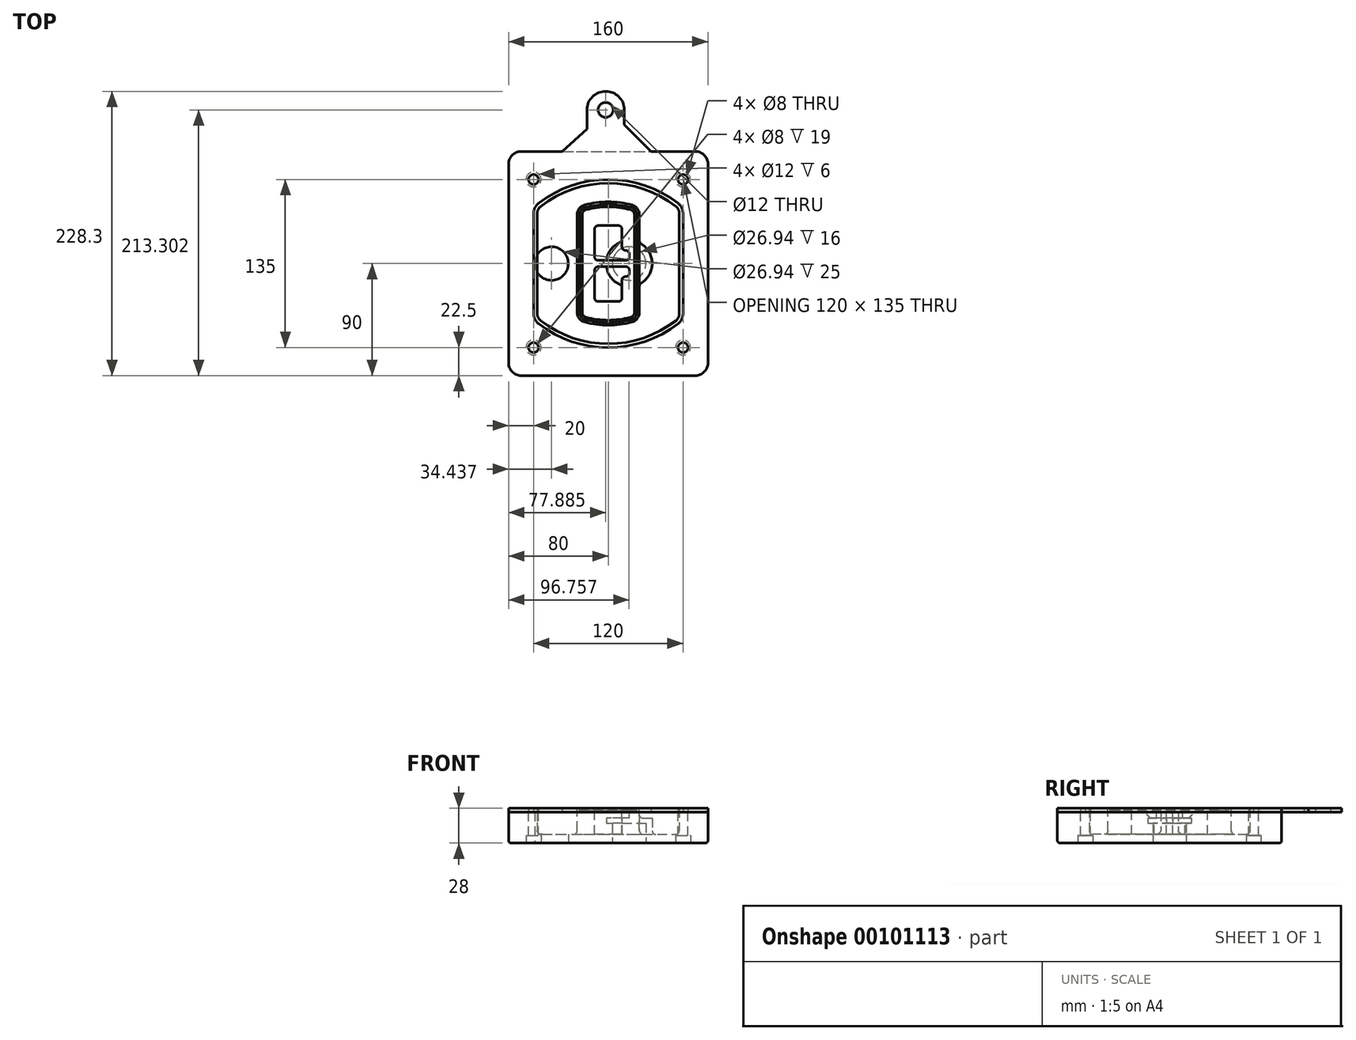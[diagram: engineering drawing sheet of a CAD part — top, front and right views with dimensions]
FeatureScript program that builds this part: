
annotation { "Feature Type Name" : "Feature", "Feature Type Description" : "" }
export const myFeature = defineFeature(function(context is Context, id is Id, definition is map)
    precondition{}
    {
        {
            var Q0;
            Q0=qCreatedBy(makeId("Top.planeOp"),FACE);
            var sketch = newSketch(context, id + "F0", { "sketchPlane" : qUnion([Q0])});
            skPoint(sketch, "E0.rect.middle", {"position": v(0, 0) * mm});
            skLineSegment(sketch, "E1.bottom", {"start": v(-70, -90) * mm, "end": v(70, -90) * mm});
            skLineSegment(sketch, "E1.top", {"start": v(-70, 90) * mm, "end": v(70, 90) * mm});
            skLineSegment(sketch, "E1.left", {"start": v(-80, -80) * mm, "end": v(-80, 80) * mm});
            skLineSegment(sketch, "E1.right", {"start": v(80, -80) * mm, "end": v(80, 80) * mm});
            skLineSegment(sketch, "E2", {"start": v(-80, 90) * mm, "end": v(80, -90) * mm, "construction": true});
            skLineSegment(sketch, "E3", {"start": v(80, 90) * mm, "end": v(-80, -90) * mm, "construction": true});
            skCircle(sketch, "E4", {"center": v(-60, 67.5) * mm, "radius": 4 * mm});
            skCircle(sketch, "E5", {"center": v(60, 67.5) * mm, "radius": 4 * mm});
            skCircle(sketch, "E6", {"center": v(60, -67.5) * mm, "radius": 4 * mm});
            skCircle(sketch, "E7", {"center": v(-60, -67.5) * mm, "radius": 4 * mm});
            skLineSegment(sketch, "E8", {"start": v(-60, 67.5) * mm, "end": v(60, 67.5) * mm, "construction": true});
            skLineSegment(sketch, "E9", {"start": v(60, 67.5) * mm, "end": v(60, -67.5) * mm, "construction": true});
            skLineSegment(sketch, "E10", {"start": v(60, -67.5) * mm, "end": v(-60, -67.5) * mm, "construction": true});
            skLineSegment(sketch, "E11", {"start": v(-60, -67.5) * mm, "end": v(-60, 67.5) * mm, "construction": true});
            skLineSegment(sketch, "E12", {"start": v(-60, 40.3) * mm, "end": v(-60, -40.3) * mm});
            skLineSegment(sketch, "E13", {"start": v(60, 40.3) * mm, "end": v(60, -40.3) * mm});
            skArc(sketch, "E14", {"start": v(56.15, 48.18) * mm, "mid": v(0, 67.5) * mm, "end": v(-56.15, 48.18) * mm});
            skArc(sketch, "E15", {"start": v(-56.15, -48.18) * mm, "mid": v(0, -67.5) * mm, "end": v(56.15, -48.18) * mm});
            skLineSegment(sketch, "E16", {"start": v(-60, 0) * mm, "end": v(60, 0) * mm, "construction": true});
            skPoint(sketch, "E17.visualSharp", {"position": v(-60, -45) * mm});
            skArc(sketch, "E17.filletArc", {"start": v(-60, -40.3) * mm, "mid": v(-58.99, -44.68) * mm, "end": v(-56.15, -48.18) * mm});
            skPoint(sketch, "E18.visualSharp", {"position": v(-60, 45) * mm});
            skArc(sketch, "E18.filletArc", {"start": v(-56.15, 48.18) * mm, "mid": v(-58.99, 44.68) * mm, "end": v(-60, 40.3) * mm});
            skPoint(sketch, "E19.visualSharp", {"position": v(60, 45) * mm});
            skArc(sketch, "E19.filletArc", {"start": v(60, 40.3) * mm, "mid": v(58.99, 44.68) * mm, "end": v(56.15, 48.18) * mm});
            skPoint(sketch, "E20.visualSharp", {"position": v(60, -45) * mm});
            skArc(sketch, "E20.filletArc", {"start": v(56.15, -48.18) * mm, "mid": v(58.99, -44.68) * mm, "end": v(60, -40.3) * mm});
            skPoint(sketch, "E21.visualSharp", {"position": v(-80, 90) * mm});
            skArc(sketch, "E21.filletArc", {"start": v(-70, 90) * mm, "mid": v(-77.07, 87.07) * mm, "end": v(-80, 80) * mm});
            skPoint(sketch, "E22.visualSharp", {"position": v(80, 90) * mm});
            skArc(sketch, "E22.filletArc", {"start": v(80, 80) * mm, "mid": v(77.07, 87.07) * mm, "end": v(70, 90) * mm});
            skPoint(sketch, "E23.visualSharp", {"position": v(80, -90) * mm});
            skArc(sketch, "E23.filletArc", {"start": v(70, -90) * mm, "mid": v(77.07, -87.07) * mm, "end": v(80, -80) * mm});
            skPoint(sketch, "E24.visualSharp", {"position": v(-80, -90) * mm});
            skArc(sketch, "E24.filletArc", {"start": v(-80, -80) * mm, "mid": v(-77.07, -87.07) * mm, "end": v(-70, -90) * mm});
            skArc(sketch, "E25.0", {"start": v(57, 40.3) * mm, "mid": v(56.3, 43.36) * mm, "end": v(54.3, 45.81) * mm});
            skLineSegment(sketch, "E25.1", {"start": v(57, 40.3) * mm, "end": v(57, -40.3) * mm});
            skArc(sketch, "E25.2", {"start": v(54.3, -45.81) * mm, "mid": v(56.3, -43.36) * mm, "end": v(57, -40.3) * mm});
            skArc(sketch, "E25.3", {"start": v(-54.3, -45.81) * mm, "mid": v(0, -64.5) * mm, "end": v(54.3, -45.81) * mm});
            skArc(sketch, "E25.4", {"start": v(-57, -40.3) * mm, "mid": v(-56.3, -43.36) * mm, "end": v(-54.3, -45.81) * mm});
            skArc(sketch, "E25.5", {"start": v(54.3, 45.81) * mm, "mid": v(0, 64.5) * mm, "end": v(-54.3, 45.81) * mm});
            skLineSegment(sketch, "E25.6", {"start": v(-57, 40.3) * mm, "end": v(-57, -40.3) * mm});
            skArc(sketch, "E25.7", {"start": v(-54.3, 45.81) * mm, "mid": v(-56.3, 43.36) * mm, "end": v(-57, 40.3) * mm});
            skArc(sketch, "E26.0", {"start": v(-58.62, 51.33) * mm, "mid": v(-62.58, 46.43) * mm, "end": v(-64, 40.3) * mm});
            skArc(sketch, "E26.1", {"start": v(58.62, 51.33) * mm, "mid": v(0, 71.5) * mm, "end": v(-58.62, 51.33) * mm});
            skArc(sketch, "E26.2", {"start": v(64, 40.3) * mm, "mid": v(62.58, 46.43) * mm, "end": v(58.62, 51.33) * mm});
            skLineSegment(sketch, "E26.3", {"start": v(64, 40.3) * mm, "end": v(64, -40.3) * mm});
            skArc(sketch, "E26.4", {"start": v(58.62, -51.33) * mm, "mid": v(62.58, -46.43) * mm, "end": v(64, -40.3) * mm});
            skLineSegment(sketch, "E26.5", {"start": v(-64, 40.3) * mm, "end": v(-64, -40.3) * mm});
            skArc(sketch, "E26.6", {"start": v(-58.62, -51.33) * mm, "mid": v(0, -71.5) * mm, "end": v(58.62, -51.33) * mm});
            skArc(sketch, "E26.7", {"start": v(-64, -40.3) * mm, "mid": v(-62.58, -46.43) * mm, "end": v(-58.62, -51.33) * mm});
            skSolve(sketch);
        }
        {
            var Q0;
            Q0=makeQuery(id+"F0.imprint","IMPRINT",FACE,{"disambiguationData":[TD([[makeQuery(id+"F0.imprint","IMPRINT",EDGE,{"derivedFrom":sQuery(id+"F0.wireOp",EDGE,"E1.bottom")}),1.0]])]});
            var Q1;
            Q1=makeQuery(id+"F0.imprint","IMPRINT",FACE,{"disambiguationData":[TD([[makeQuery(id+"F0.imprint","IMPRINT",EDGE,{"derivedFrom":sQuery(id+"F0.wireOp",EDGE,"E12")}),1.0]])]});
            var Q2;
            Q2=makeQuery(id+"F0.imprint","IMPRINT",FACE,{"disambiguationData":[TD([[makeQuery(id+"F0.imprint","IMPRINT",EDGE,{"derivedFrom":sQuery(id+"F0.wireOp",EDGE,"E25.0")}),1.0]])]});
            var Q3;
            Q3=makeQuery(id+"F0.imprint","IMPRINT",FACE,{"disambiguationData":[TD([[makeQuery(id+"F0.imprint","IMPRINT",EDGE,{"derivedFrom":sQuery(id+"F0.wireOp",EDGE,"E12")}),-1.0]])]});
            extrude(context, id + "F1", {"entities" : qUnion([Q0, Q1, Q2, Q3]), "oppositeDirection" : true, "depth" : 25 * mm});
        }
        {
            var Q0;
            Q0=makeQuery(id+"F0.imprint","IMPRINT",FACE,{"disambiguationData":[TD([[makeQuery(id+"F0.imprint","IMPRINT",EDGE,{"derivedFrom":sQuery(id+"F0.wireOp",EDGE,"E12")}),1.0]])]});
            extrude(context, id + "F2", {"entities" : qUnion([Q0]), "operationType" : NewBodyOperationType.ADD, "depth" : 3 * mm});
        }
        {
            var Q0;
            Q0=makeQuery(id+"F0.imprint","IMPRINT",FACE,{"disambiguationData":[TD([[makeQuery(id+"F0.imprint","IMPRINT",EDGE,{"derivedFrom":sQuery(id+"F0.wireOp",EDGE,"E25.0")}),1.0]])]});
            extrude(context, id + "F3", {"entities" : qUnion([Q0]), "operationType" : NewBodyOperationType.REMOVE, "oppositeDirection" : true, "depth" : 18 * mm});
        }
        {
            var Q0;
            Q0=makeQuery(id+"F2.opExtrude","CAP_FACE",FACE,{"disambiguationData":[OSD([sQuery(id+"F0.wireOp",EDGE,"E12"),sQuery(id+"F0.wireOp",EDGE,"E13"),sQuery(id+"F0.wireOp",EDGE,"E14"),sQuery(id+"F0.wireOp",EDGE,"E15"),sQuery(id+"F0.wireOp",EDGE,"E17.filletArc"),sQuery(id+"F0.wireOp",EDGE,"E18.filletArc"),sQuery(id+"F0.wireOp",EDGE,"E19.filletArc"),sQuery(id+"F0.wireOp",EDGE,"E20.filletArc"),sQuery(id+"F0.wireOp",EDGE,"E25.0"),sQuery(id+"F0.wireOp",EDGE,"E25.1"),sQuery(id+"F0.wireOp",EDGE,"E25.2"),sQuery(id+"F0.wireOp",EDGE,"E25.3"),sQuery(id+"F0.wireOp",EDGE,"E25.4"),sQuery(id+"F0.wireOp",EDGE,"E25.5"),sQuery(id+"F0.wireOp",EDGE,"E25.6"),sQuery(id+"F0.wireOp",EDGE,"E25.7")])],"isStart":false});
            var sketch = newSketch(context, id + "F4", { "sketchPlane" : qUnion([Q0])});
            skArc(sketch, "E27.0", {"start": v(-19.08, -46.97) * mm, "mid": v(0, -49.5) * mm, "end": v(19.08, -46.97) * mm});
            skArc(sketch, "E28.0", {"start": v(19.08, 46.97) * mm, "mid": v(0, 49.5) * mm, "end": v(-19.08, 46.97) * mm});
            skLineSegment(sketch, "E29", {"start": v(-25, 39.25) * mm, "end": v(-25, -39.25) * mm});
            skLineSegment(sketch, "E30", {"start": v(25, 39.25) * mm, "end": v(25, -39.25) * mm});
            skLineSegment(sketch, "E31", {"start": v(-25, 45.1) * mm, "end": v(25, 45.1) * mm, "construction": true});
            skLineSegment(sketch, "E32", {"start": v(-25, -45.1) * mm, "end": v(25, -45.1) * mm, "construction": true});
            skPoint(sketch, "E33.visualSharp", {"position": v(-25, 45.1) * mm});
            skArc(sketch, "E33.filletArc", {"start": v(-19.08, 46.97) * mm, "mid": v(-23.35, 44.11) * mm, "end": v(-25, 39.25) * mm});
            skPoint(sketch, "E34.visualSharp", {"position": v(25, 45.1) * mm});
            skArc(sketch, "E34.filletArc", {"start": v(25, 39.25) * mm, "mid": v(23.35, 44.11) * mm, "end": v(19.08, 46.97) * mm});
            skPoint(sketch, "E35.visualSharp", {"position": v(25, -45.1) * mm});
            skArc(sketch, "E35.filletArc", {"start": v(19.08, -46.97) * mm, "mid": v(23.35, -44.11) * mm, "end": v(25, -39.25) * mm});
            skPoint(sketch, "E36.visualSharp", {"position": v(-25, -45.1) * mm});
            skArc(sketch, "E36.filletArc", {"start": v(-25, -39.25) * mm, "mid": v(-23.35, -44.11) * mm, "end": v(-19.08, -46.97) * mm});
            skArc(sketch, "E37.0", {"start": v(54.3, 45.81) * mm, "mid": v(0, 64.5) * mm, "end": v(-54.3, 45.81) * mm});
            skArc(sketch, "E37.1", {"start": v(-54.3, 45.81) * mm, "mid": v(-56.3, 43.36) * mm, "end": v(-57, 40.3) * mm});
            skLineSegment(sketch, "E37.2", {"start": v(-57, 40.3) * mm, "end": v(-57, -40.3) * mm});
            skArc(sketch, "E37.3", {"start": v(-57, -40.3) * mm, "mid": v(-56.3, -43.36) * mm, "end": v(-54.3, -45.81) * mm});
            skArc(sketch, "E37.4", {"start": v(-54.3, -45.81) * mm, "mid": v(0, -64.5) * mm, "end": v(54.3, -45.81) * mm});
            skArc(sketch, "E37.5", {"start": v(54.3, -45.81) * mm, "mid": v(56.3, -43.36) * mm, "end": v(57, -40.3) * mm});
            skLineSegment(sketch, "E37.6", {"start": v(57, 40.3) * mm, "end": v(57, -40.3) * mm});
            skArc(sketch, "E37.7", {"start": v(57, 40.3) * mm, "mid": v(56.3, 43.36) * mm, "end": v(54.3, 45.81) * mm});
            skLineSegment(sketch, "E38.0", {"start": v(23, 39.25) * mm, "end": v(23, -39.25) * mm});
            skArc(sketch, "E38.1", {"start": v(18.56, -45.04) * mm, "mid": v(21.76, -42.9) * mm, "end": v(23, -39.25) * mm});
            skArc(sketch, "E38.2", {"start": v(-18.56, -45.04) * mm, "mid": v(0, -47.5) * mm, "end": v(18.56, -45.04) * mm});
            skArc(sketch, "E38.3", {"start": v(-23, -39.25) * mm, "mid": v(-21.76, -42.9) * mm, "end": v(-18.56, -45.04) * mm});
            skLineSegment(sketch, "E38.4", {"start": v(-23, 39.25) * mm, "end": v(-23, -39.25) * mm});
            skArc(sketch, "E38.5", {"start": v(23, 39.25) * mm, "mid": v(21.76, 42.9) * mm, "end": v(18.56, 45.04) * mm});
            skArc(sketch, "E38.6", {"start": v(-18.56, 45.04) * mm, "mid": v(-21.76, 42.9) * mm, "end": v(-23, 39.25) * mm});
            skArc(sketch, "E38.7", {"start": v(18.56, 45.04) * mm, "mid": v(0, 47.5) * mm, "end": v(-18.56, 45.04) * mm});
            skArc(sketch, "E39.0", {"start": v(21, 39.25) * mm, "mid": v(20.18, 41.68) * mm, "end": v(18.04, 43.1) * mm});
            skLineSegment(sketch, "E39.1", {"start": v(21, 39.25) * mm, "end": v(21, -39.25) * mm});
            skArc(sketch, "E39.2", {"start": v(18.04, -43.1) * mm, "mid": v(20.18, -41.68) * mm, "end": v(21, -39.25) * mm});
            skArc(sketch, "E39.3", {"start": v(-18.04, -43.1) * mm, "mid": v(0, -45.5) * mm, "end": v(18.04, -43.1) * mm});
            skArc(sketch, "E39.4", {"start": v(-21, -39.25) * mm, "mid": v(-20.18, -41.68) * mm, "end": v(-18.04, -43.1) * mm});
            skArc(sketch, "E39.5", {"start": v(18.04, 43.1) * mm, "mid": v(0, 45.5) * mm, "end": v(-18.04, 43.1) * mm});
            skLineSegment(sketch, "E39.6", {"start": v(-21, 39.25) * mm, "end": v(-21, -39.25) * mm});
            skArc(sketch, "E39.7", {"start": v(-18.04, 43.1) * mm, "mid": v(-20.18, 41.68) * mm, "end": v(-21, 39.25) * mm});
            skLineSegment(sketch, "E40", {"start": v(-25, 0) * mm, "end": v(25, 0) * mm, "construction": true});
            skLineSegment(sketch, "E41", {"start": v(-11, 5.5) * mm, "end": v(-11, 27.5) * mm});
            skLineSegment(sketch, "E42", {"start": v(-8, 30.5) * mm, "end": v(8, 30.5) * mm});
            skLineSegment(sketch, "E43", {"start": v(11, 27.5) * mm, "end": v(11, 13.5) * mm});
            skLineSegment(sketch, "E44", {"start": v(14, 10.5) * mm, "end": v(14, 10.5) * mm});
            skLineSegment(sketch, "E45", {"start": v(17, 7.5) * mm, "end": v(17, 5.5) * mm});
            skLineSegment(sketch, "E46", {"start": v(14, 2.5) * mm, "end": v(-8, 2.5) * mm});
            skPoint(sketch, "E47.visualSharp", {"position": v(-11, 30.5) * mm});
            skArc(sketch, "E47.filletArc", {"start": v(-8, 30.5) * mm, "mid": v(-10.12, 29.62) * mm, "end": v(-11, 27.5) * mm});
            skPoint(sketch, "E48.visualSharp", {"position": v(11, 30.5) * mm});
            skArc(sketch, "E48.filletArc", {"start": v(11, 27.5) * mm, "mid": v(10.12, 29.62) * mm, "end": v(8, 30.5) * mm});
            skPoint(sketch, "E49.visualSharp", {"position": v(11, 10.5) * mm});
            skArc(sketch, "E49.filletArc", {"start": v(11, 13.5) * mm, "mid": v(11.88, 11.38) * mm, "end": v(14, 10.5) * mm});
            skPoint(sketch, "E50.visualSharp", {"position": v(17, 10.5) * mm});
            skArc(sketch, "E50.filletArc", {"start": v(17, 7.5) * mm, "mid": v(16.12, 9.62) * mm, "end": v(14, 10.5) * mm});
            skPoint(sketch, "E51.visualSharp", {"position": v(17, 2.5) * mm});
            skArc(sketch, "E51.filletArc", {"start": v(14, 2.5) * mm, "mid": v(16.12, 3.38) * mm, "end": v(17, 5.5) * mm});
            skPoint(sketch, "E52.visualSharp", {"position": v(-11, 2.5) * mm});
            skArc(sketch, "E52.filletArc", {"start": v(-11, 5.5) * mm, "mid": v(-10.12, 3.38) * mm, "end": v(-8, 2.5) * mm});
            skLineSegment(sketch, "E53.0.MirrorCS", {"start": v(14, -2.5) * mm, "end": v(-8, -2.5) * mm});
            skArc(sketch, "E54.0.MirrorCS", {"start": v(-11, -5.5) * mm, "mid": v(-10.12, -3.38) * mm, "end": v(-8, -2.5) * mm});
            skLineSegment(sketch, "E55.0.MirrorCS", {"start": v(-11, -5.5) * mm, "end": v(-11, -27.5) * mm});
            skArc(sketch, "E56.0.MirrorCS", {"start": v(-8, -30.5) * mm, "mid": v(-10.12, -29.62) * mm, "end": v(-11, -27.5) * mm});
            skLineSegment(sketch, "E57.0.MirrorCS", {"start": v(-8, -30.5) * mm, "end": v(8, -30.5) * mm});
            skArc(sketch, "E58.0.MirrorCS", {"start": v(11, -27.5) * mm, "mid": v(10.12, -29.62) * mm, "end": v(8, -30.5) * mm});
            skLineSegment(sketch, "E59.0.MirrorCS", {"start": v(11, -27.5) * mm, "end": v(11, -13.5) * mm});
            skArc(sketch, "E60.0.MirrorCS", {"start": v(11, -13.5) * mm, "mid": v(11.88, -11.38) * mm, "end": v(14, -10.5) * mm});
            skArc(sketch, "E61.0.MirrorCS", {"start": v(17, -7.5) * mm, "mid": v(16.12, -9.62) * mm, "end": v(14, -10.5) * mm});
            skLineSegment(sketch, "E62.0.MirrorCS", {"start": v(17, -7.5) * mm, "end": v(17, -5.5) * mm});
            skArc(sketch, "E63.0.MirrorCS", {"start": v(14, -2.5) * mm, "mid": v(16.12, -3.38) * mm, "end": v(17, -5.5) * mm});
            skSolve(sketch);
        }
        {
            var Q0;
            Q0=makeQuery(id+"F4.imprint","IMPRINT",FACE,{"disambiguationData":[TD([[makeQuery(id+"F4.imprint","IMPRINT",EDGE,{"derivedFrom":sQuery(id+"F4.wireOp",EDGE,"E27.0")}),1.0]])]});
            var Q1;
            Q1=makeQuery(id+"F4.imprint","IMPRINT",FACE,{"disambiguationData":[TD([[makeQuery(id+"F4.imprint","IMPRINT",EDGE,{"derivedFrom":sQuery(id+"F4.wireOp",EDGE,"E38.0")}),-1.0]])]});
            var Q2;
            Q2=makeQuery(id+"F4.imprint","IMPRINT",FACE,{"disambiguationData":[TD([[makeQuery(id+"F4.imprint","IMPRINT",EDGE,{"derivedFrom":sQuery(id+"F4.wireOp",EDGE,"E39.0")}),1.0]])]});
            extrude(context, id + "F5", {"entities" : qUnion([Q0, Q1, Q2]), "operationType" : NewBodyOperationType.ADD, "endBound" : BoundingType.UP_TO_NEXT, "oppositeDirection" : true, "depth" : 25 * mm});
        }
        {
            var Q0;
            Q0=makeQuery(id+"F4.imprint","IMPRINT",FACE,{"disambiguationData":[TD([[makeQuery(id+"F4.imprint","IMPRINT",EDGE,{"derivedFrom":sQuery(id+"F4.wireOp",EDGE,"E38.0")}),-1.0]])]});
            extrude(context, id + "F6", {"entities" : qUnion([Q0]), "operationType" : NewBodyOperationType.REMOVE, "oppositeDirection" : true, "depth" : 2 * mm});
        }
        {
            var Q0;
            Q0=makeQuery(id+"F1.opExtrude","CAP_FACE",FACE,{"disambiguationData":[OSD([sQuery(id+"F0.wireOp",EDGE,"E1.bottom"),sQuery(id+"F0.wireOp",EDGE,"E1.top"),sQuery(id+"F0.wireOp",EDGE,"E1.left"),sQuery(id+"F0.wireOp",EDGE,"E1.right"),sQuery(id+"F0.wireOp",EDGE,"E4"),sQuery(id+"F0.wireOp",EDGE,"E5"),sQuery(id+"F0.wireOp",EDGE,"E6"),sQuery(id+"F0.wireOp",EDGE,"E7"),sQuery(id+"F0.wireOp",EDGE,"E21.filletArc"),sQuery(id+"F0.wireOp",EDGE,"E22.filletArc"),sQuery(id+"F0.wireOp",EDGE,"E23.filletArc"),sQuery(id+"F0.wireOp",EDGE,"E24.filletArc")])],"isStart":false});
            var sketch = newSketch(context, id + "F7", { "sketchPlane" : qUnion([Q0])});
            skCircle(sketch, "E64", {"center": v(16.76, 0) * mm, "radius": 13.47 * mm});
            skCircle(sketch, "E65", {"center": v(-45.56, 0) * mm, "radius": 13.47 * mm});
            skLineSegment(sketch, "E66", {"start": v(80, 0) * mm, "end": v(-80, 0) * mm});
            skCircle(sketch, "E67", {"center": v(16.76, 0) * mm, "radius": 18.47 * mm});
            skCircle(sketch, "E68", {"center": v(60, -67.5) * mm, "radius": 6 * mm});
            skCircle(sketch, "E69", {"center": v(-60, -67.5) * mm, "radius": 6 * mm});
            skCircle(sketch, "E70", {"center": v(-60, 67.5) * mm, "radius": 6 * mm});
            skCircle(sketch, "E71", {"center": v(60, 67.5) * mm, "radius": 6 * mm});
            skSolve(sketch);
        }
        {
            var Q0;
            {var subQ1=sQuery(id+"F7.wireOp",EDGE,"E66");var subQ4=sQuery(id+"F7.wireOp",EDGE,"E64");var subQ6=makeQuery(id+"F7.imprint","INTERSECT",VERTEX,{"disambiguationData":[OD(0.0)],"derivedFrom":[subQ4,subQ1]});Q0=makeQuery(id+"F7.imprint","IMPRINT",FACE,{"disambiguationData":[TD([[makeQuery(id+"F7.imprint","IMPRINT",EDGE,{"disambiguationData":[TD([[subQ6,-1.0]])],"derivedFrom":subQ4}),-1.0]])]});}
            var Q1;
            {var subQ0=sQuery(id+"F7.wireOp",EDGE,"E66");var subQ1=sQuery(id+"F7.wireOp",EDGE,"E64");var subQ3=makeQuery(id+"F7.imprint","INTERSECT",VERTEX,{"disambiguationData":[OD(0.0)],"derivedFrom":[subQ1,subQ0]});Q1=makeQuery(id+"F7.imprint","IMPRINT",FACE,{"disambiguationData":[TD([[makeQuery(id+"F7.imprint","IMPRINT",EDGE,{"disambiguationData":[TD([[subQ3,-1.0]])],"derivedFrom":subQ1}),1.0]])]});}
            var Q2;
            {var subQ0=sQuery(id+"F7.wireOp",EDGE,"E66");var subQ1=sQuery(id+"F7.wireOp",EDGE,"E64");var subQ3=makeQuery(id+"F7.imprint","INTERSECT",VERTEX,{"disambiguationData":[OD(0.0)],"derivedFrom":[subQ1,subQ0]});Q2=makeQuery(id+"F7.imprint","IMPRINT",FACE,{"disambiguationData":[TD([[makeQuery(id+"F7.imprint","IMPRINT",EDGE,{"disambiguationData":[TD([[subQ3,1.0]])],"derivedFrom":subQ1}),1.0]])]});}
            var Q3;
            {var subQ1=sQuery(id+"F7.wireOp",EDGE,"E66");var subQ4=sQuery(id+"F7.wireOp",EDGE,"E64");var subQ6=makeQuery(id+"F7.imprint","INTERSECT",VERTEX,{"disambiguationData":[OD(0.0)],"derivedFrom":[subQ4,subQ1]});Q3=makeQuery(id+"F7.imprint","IMPRINT",FACE,{"disambiguationData":[TD([[makeQuery(id+"F7.imprint","IMPRINT",EDGE,{"disambiguationData":[TD([[subQ6,1.0]])],"derivedFrom":subQ4}),-1.0]])]});}
            extrude(context, id + "F8", {"entities" : qUnion([Q0, Q1, Q2, Q3]), "operationType" : NewBodyOperationType.ADD, "oppositeDirection" : true, "depth" : 20 * mm});
        }
        {
            var Q0;
            {var subQ0=sQuery(id+"F7.wireOp",EDGE,"E66");var subQ1=sQuery(id+"F7.wireOp",EDGE,"E64");var subQ3=makeQuery(id+"F7.imprint","INTERSECT",VERTEX,{"disambiguationData":[OD(0.0)],"derivedFrom":[subQ1,subQ0]});Q0=makeQuery(id+"F7.imprint","IMPRINT",FACE,{"disambiguationData":[TD([[makeQuery(id+"F7.imprint","IMPRINT",EDGE,{"disambiguationData":[TD([[subQ3,-1.0]])],"derivedFrom":subQ1}),1.0]])]});}
            var Q1;
            {var subQ0=sQuery(id+"F7.wireOp",EDGE,"E66");var subQ1=sQuery(id+"F7.wireOp",EDGE,"E64");var subQ3=makeQuery(id+"F7.imprint","INTERSECT",VERTEX,{"disambiguationData":[OD(0.0)],"derivedFrom":[subQ1,subQ0]});Q1=makeQuery(id+"F7.imprint","IMPRINT",FACE,{"disambiguationData":[TD([[makeQuery(id+"F7.imprint","IMPRINT",EDGE,{"disambiguationData":[TD([[subQ3,1.0]])],"derivedFrom":subQ1}),1.0]])]});}
            extrude(context, id + "F9", {"entities" : qUnion([Q0, Q1]), "operationType" : NewBodyOperationType.REMOVE, "oppositeDirection" : true, "depth" : 16 * mm});
        }
        {
            var Q0;
            {var subQ0=sQuery(id+"F7.wireOp",EDGE,"E66");var subQ1=sQuery(id+"F7.wireOp",EDGE,"E65");var subQ3=makeQuery(id+"F7.imprint","INTERSECT",VERTEX,{"disambiguationData":[OD(0.0)],"derivedFrom":[subQ1,subQ0]});Q0=makeQuery(id+"F7.imprint","IMPRINT",FACE,{"disambiguationData":[TD([[makeQuery(id+"F7.imprint","IMPRINT",EDGE,{"disambiguationData":[TD([[subQ3,-1.0]])],"derivedFrom":subQ1}),1.0]])]});}
            var Q1;
            {var subQ0=sQuery(id+"F7.wireOp",EDGE,"E66");var subQ1=sQuery(id+"F7.wireOp",EDGE,"E65");var subQ3=makeQuery(id+"F7.imprint","INTERSECT",VERTEX,{"disambiguationData":[OD(0.0)],"derivedFrom":[subQ1,subQ0]});Q1=makeQuery(id+"F7.imprint","IMPRINT",FACE,{"disambiguationData":[TD([[makeQuery(id+"F7.imprint","IMPRINT",EDGE,{"disambiguationData":[TD([[subQ3,1.0]])],"derivedFrom":subQ1}),1.0]])]});}
            extrude(context, id + "F10", {"entities" : qUnion([Q0, Q1]), "operationType" : NewBodyOperationType.REMOVE, "oppositeDirection" : true, "depth" : 25 * mm});
        }
        {
            var Q0;
            Q0=makeQuery(id+"F7.imprint","IMPRINT",FACE,{"disambiguationData":[TD([[makeQuery(id+"F7.imprint","IMPRINT",EDGE,{"derivedFrom":sQuery(id+"F7.wireOp",EDGE,"E68")}),1.0]])]});
            var Q1;
            Q1=makeQuery(id+"F7.imprint","IMPRINT",FACE,{"disambiguationData":[TD([[makeQuery(id+"F7.imprint","IMPRINT",EDGE,{"derivedFrom":makeQuery(id+"F1.opExtrude","CAP_EDGE",EDGE,{"disambiguationData":[OSD([sQuery(id+"F0.wireOp",EDGE,"E5")])],"isStart":false})}),-1.0]])]});
            var Q2;
            Q2=makeQuery(id+"F7.imprint","IMPRINT",FACE,{"disambiguationData":[TD([[makeQuery(id+"F7.imprint","IMPRINT",EDGE,{"derivedFrom":sQuery(id+"F7.wireOp",EDGE,"E69")}),1.0]])]});
            var Q3;
            Q3=makeQuery(id+"F7.imprint","IMPRINT",FACE,{"disambiguationData":[TD([[makeQuery(id+"F7.imprint","IMPRINT",EDGE,{"derivedFrom":makeQuery(id+"F1.opExtrude","CAP_EDGE",EDGE,{"disambiguationData":[OSD([sQuery(id+"F0.wireOp",EDGE,"E4")])],"isStart":false})}),-1.0]])]});
            var Q4;
            Q4=makeQuery(id+"F7.imprint","IMPRINT",FACE,{"disambiguationData":[TD([[makeQuery(id+"F7.imprint","IMPRINT",EDGE,{"derivedFrom":sQuery(id+"F7.wireOp",EDGE,"E70")}),1.0]])]});
            var Q5;
            Q5=makeQuery(id+"F7.imprint","IMPRINT",FACE,{"disambiguationData":[TD([[makeQuery(id+"F7.imprint","IMPRINT",EDGE,{"derivedFrom":makeQuery(id+"F1.opExtrude","CAP_EDGE",EDGE,{"disambiguationData":[OSD([sQuery(id+"F0.wireOp",EDGE,"E7")])],"isStart":false})}),-1.0]])]});
            var Q6;
            Q6=makeQuery(id+"F7.imprint","IMPRINT",FACE,{"disambiguationData":[TD([[makeQuery(id+"F7.imprint","IMPRINT",EDGE,{"derivedFrom":sQuery(id+"F7.wireOp",EDGE,"E71")}),1.0]])]});
            var Q7;
            Q7=makeQuery(id+"F7.imprint","IMPRINT",FACE,{"disambiguationData":[TD([[makeQuery(id+"F7.imprint","IMPRINT",EDGE,{"derivedFrom":makeQuery(id+"F1.opExtrude","CAP_EDGE",EDGE,{"disambiguationData":[OSD([sQuery(id+"F0.wireOp",EDGE,"E6")])],"isStart":false})}),-1.0]])]});
            extrude(context, id + "F11", {"entities" : qUnion([Q0, Q1, Q2, Q3, Q4, Q5, Q6, Q7]), "operationType" : NewBodyOperationType.REMOVE, "oppositeDirection" : true, "depth" : 6 * mm});
        }
        {
            var Q0;
            Q0=makeQuery(id+"F9.boolean.opBoolean","COPY",FACE,{"derivedFrom":makeQuery(id+"F9.opExtrude","CAP_FACE",FACE,{"disambiguationData":[OSD([sQuery(id+"F7.wireOp",EDGE,"E64")])],"isStart":false})});
            var sketch = newSketch(context, id + "F12", { "sketchPlane" : qUnion([Q0])});
            skArc(sketch, "E72.0", {"start": v(11, 17.55) * mm, "mid": v(2.57, 11.82) * mm, "end": v(-1.54, 2.5) * mm});
            skArc(sketch, "E72.1", {"start": v(-1.54, -2.5) * mm, "mid": v(2.57, -11.82) * mm, "end": v(11, -17.55) * mm});
            skLineSegment(sketch, "E73", {"start": v(-1.54, -2.5) * mm, "end": v(14, -2.5) * mm});
            skLineSegment(sketch, "E74.0", {"start": v(14, 2.5) * mm, "end": v(-1.54, 2.5) * mm});
            skArc(sketch, "E74.1", {"start": v(14, 2.5) * mm, "mid": v(16.12, 3.38) * mm, "end": v(17, 5.5) * mm});
            skLineSegment(sketch, "E74.2", {"start": v(17, 7.5) * mm, "end": v(17, 5.5) * mm});
            skArc(sketch, "E74.3", {"start": v(17, 7.5) * mm, "mid": v(16.12, 9.62) * mm, "end": v(14, 10.5) * mm});
            skArc(sketch, "E74.4", {"start": v(11, 13.5) * mm, "mid": v(11.88, 11.38) * mm, "end": v(14, 10.5) * mm});
            skLineSegment(sketch, "E74.5", {"start": v(11, 17.55) * mm, "end": v(11, 13.5) * mm});
            skLineSegment(sketch, "E74.7", {"start": v(14, -2.5) * mm, "end": v(-1.54, -2.5) * mm});
            skArc(sketch, "E74.8", {"start": v(14, -2.5) * mm, "mid": v(16.12, -3.38) * mm, "end": v(17, -5.5) * mm});
            skLineSegment(sketch, "E74.9", {"start": v(17, -7.5) * mm, "end": v(17, -5.5) * mm});
            skArc(sketch, "E74.10", {"start": v(17, -7.5) * mm, "mid": v(16.12, -9.62) * mm, "end": v(14, -10.5) * mm});
            skArc(sketch, "E74.11", {"start": v(11, -13.5) * mm, "mid": v(11.88, -11.38) * mm, "end": v(14, -10.5) * mm});
            skLineSegment(sketch, "E74.12", {"start": v(11, -17.55) * mm, "end": v(11, -13.5) * mm});
            skPoint(sketch, "E75.orphan", {"position": v(11, -27.5) * mm});
            skPoint(sketch, "E76.orphan", {"position": v(-8, -2.5) * mm});
            skPoint(sketch, "E77.orphan", {"position": v(-8, 2.5) * mm});
            skPoint(sketch, "E78.orphan", {"position": v(11, 27.5) * mm});
            skSolve(sketch);
        }
        {
            var Q0;
            {var subQ7=sQuery(id+"F12.wireOp",EDGE,"E72.0");var subQ14=sQuery(id+"F12.wireOp",EDGE,"E72.1");var subQ16=sQuery(id+"F12.wireOp",EDGE,"E74.1");var subQ18=sQuery(id+"F12.wireOp",EDGE,"E74.8");Q0=qUnion([makeQuery(id+"F12.imprint","IMPRINT",FACE,{"disambiguationData":[TD([[makeQuery(id+"F12.imprint","IMPRINT",EDGE,{"derivedFrom":subQ7}),1.0]])]}),makeQuery(id+"F12.imprint","IMPRINT",FACE,{"disambiguationData":[TD([[makeQuery(id+"F12.imprint","IMPRINT",EDGE,{"derivedFrom":subQ14}),1.0]])]}),makeQuery(id+"F12.imprint","IMPRINT",FACE,{"disambiguationData":[TD([[makeQuery(id+"F12.imprint","IMPRINT",EDGE,{"derivedFrom":subQ16}),1.0]])]}),makeQuery(id+"F12.imprint","IMPRINT",FACE,{"disambiguationData":[TD([[makeQuery(id+"F12.imprint","IMPRINT",EDGE,{"derivedFrom":subQ18}),-1.0]])]})]);}
            var Q1;
            Q1=makeQuery(id+"F5.boolean.opBoolean","SPLIT",FACE,{"disambiguationData":[TD([makeQuery(id+"F5.opExtrude","SWEPT_FACE",FACE,{"disambiguationData":[OSD([sQuery(id+"F4.wireOp",EDGE,"E41")])]})])],"derivedFrom":makeQuery(id+"F3.boolean.opBoolean","COPY",FACE,{"derivedFrom":makeQuery(id+"F3.opExtrude","CAP_FACE",FACE,{"disambiguationData":[OSD([sQuery(id+"F0.wireOp",EDGE,"E25.0"),sQuery(id+"F0.wireOp",EDGE,"E25.1"),sQuery(id+"F0.wireOp",EDGE,"E25.2"),sQuery(id+"F0.wireOp",EDGE,"E25.3"),sQuery(id+"F0.wireOp",EDGE,"E25.4"),sQuery(id+"F0.wireOp",EDGE,"E25.5"),sQuery(id+"F0.wireOp",EDGE,"E25.6"),sQuery(id+"F0.wireOp",EDGE,"E25.7")])],"isStart":false})})});
            extrude(context, id + "F13", {"entities" : qUnion([Q0]), "operationType" : NewBodyOperationType.REMOVE, "endBound" : BoundingType.UP_TO_SURFACE, "endBoundEntityFace" : qUnion([Q1]), "depth" : 25 * mm});
        }
        {
            var Q0;
            Q0=makeQuery(id+"F3.boolean.opBoolean","COPY",EDGE,{"derivedFrom":makeQuery(id+"F3.opExtrude","CAP_EDGE",EDGE,{"disambiguationData":[OSD([sQuery(id+"F0.wireOp",EDGE,"E25.6")])],"isStart":false})});
            var Q1;
            Q1=makeQuery(id+"F8.boolean.opBoolean","INTERSECT",EDGE,{"derivedFrom":[makeQuery(id+"F5.opExtrude","SWEPT_FACE",FACE,{"disambiguationData":[OSD([sQuery(id+"F4.wireOp",EDGE,"E30")])]}),makeQuery(id+"F8.opExtrude","CAP_FACE",FACE,{"disambiguationData":[OSD([sQuery(id+"F7.wireOp",EDGE,"E67")])],"isStart":false})]});
            var Q2;
            Q2=makeQuery(id+"F8.boolean.opBoolean","INTERSECT",EDGE,{"disambiguationData":[OD(1.0)],"derivedFrom":[makeQuery(id+"F5.opExtrude","SWEPT_FACE",FACE,{"disambiguationData":[OSD([sQuery(id+"F4.wireOp",EDGE,"E30")])]}),makeQuery(id+"F8.opExtrude","SWEPT_FACE",FACE,{"disambiguationData":[OSD([sQuery(id+"F7.wireOp",EDGE,"E67")])]})]});
            var Q3;
            {var subQ0=sQuery(id+"F4.wireOp",EDGE,"E30");Q3=makeQuery(id+"F8.boolean.opBoolean","SPLIT",EDGE,{"disambiguationData":[TD([makeQuery(id+"F5.opExtrude","SWEPT_FACE",FACE,{"disambiguationData":[OSD([sQuery(id+"F4.wireOp",EDGE,"E35.filletArc")])]})])],"derivedFrom":makeQuery(id+"F5.opExtrude","CAP_EDGE",EDGE,{"disambiguationData":[OSD([subQ0])],"isStart":false})});}
            var Q4;
            {var subQ0=sQuery(id+"F0.wireOp",EDGE,"E25.7");var subQ1=sQuery(id+"F0.wireOp",EDGE,"E25.1");var subQ2=sQuery(id+"F0.wireOp",EDGE,"E25.6");var subQ3=sQuery(id+"F0.wireOp",EDGE,"E25.5");var subQ4=sQuery(id+"F0.wireOp",EDGE,"E25.4");var subQ5=sQuery(id+"F0.wireOp",EDGE,"E25.0");var subQ6=sQuery(id+"F0.wireOp",EDGE,"E25.2");var subQ7=sQuery(id+"F0.wireOp",EDGE,"E25.3");Q4=makeQuery(id+"F8.boolean.opBoolean","INTERSECT",EDGE,{"derivedFrom":[makeQuery(id+"F5.boolean.opBoolean","SPLIT",FACE,{"disambiguationData":[TD([makeQuery(id+"F2.opExtrude","SWEPT_FACE",FACE,{"disambiguationData":[OSD([subQ5])]})])],"derivedFrom":makeQuery(id+"F3.boolean.opBoolean","COPY",FACE,{"derivedFrom":makeQuery(id+"F3.opExtrude","CAP_FACE",FACE,{"disambiguationData":[OSD([subQ5,subQ1,subQ6,subQ7,subQ4,subQ3,subQ2,subQ0])],"isStart":false})})}),makeQuery(id+"F8.opExtrude","SWEPT_FACE",FACE,{"disambiguationData":[OSD([sQuery(id+"F7.wireOp",EDGE,"E67")])]})]});}
            var Q5;
            Q5=makeQuery(id+"F8.boolean.opBoolean","INTERSECT",EDGE,{"disambiguationData":[OD(0.0)],"derivedFrom":[makeQuery(id+"F5.opExtrude","SWEPT_FACE",FACE,{"disambiguationData":[OSD([sQuery(id+"F4.wireOp",EDGE,"E30")])]}),makeQuery(id+"F8.opExtrude","SWEPT_FACE",FACE,{"disambiguationData":[OSD([sQuery(id+"F7.wireOp",EDGE,"E67")])]})]});
            fillet(context, id + "F14", {"entities" : qUnion([Q0, Q1, Q2, Q3, Q4, Q5]), "radius" : 3 * mm, "tangentPropagation" : true, "allowEdgeOverflow" : false});
        }
        {
            var Q0;
            Q0=makeQuery(id+"F1.opExtrude","CAP_EDGE",EDGE,{"disambiguationData":[OSD([sQuery(id+"F0.wireOp",EDGE,"E1.bottom")])],"isStart":false});
            fillet(context, id + "F15", {"entities" : qUnion([Q0]), "radius" : 2 * mm, "tangentPropagation" : true, "allowEdgeOverflow" : false});
        }
        {
            var Q0;
            {var subQ0=sQuery(id+"F0.wireOp",EDGE,"E22.filletArc");var subQ1=sQuery(id+"F0.wireOp",EDGE,"E7");var subQ2=sQuery(id+"F0.wireOp",EDGE,"E6");var subQ3=sQuery(id+"F0.wireOp",EDGE,"E5");var subQ4=sQuery(id+"F0.wireOp",EDGE,"E4");var subQ5=sQuery(id+"F0.wireOp",EDGE,"E1.bottom");var subQ6=sQuery(id+"F0.wireOp",EDGE,"E21.filletArc");var subQ7=sQuery(id+"F0.wireOp",EDGE,"E1.top");var subQ8=sQuery(id+"F0.wireOp",EDGE,"E1.left");var subQ9=sQuery(id+"F0.wireOp",EDGE,"E1.right");var subQ10=sQuery(id+"F0.wireOp",EDGE,"E23.filletArc");var subQ11=sQuery(id+"F0.wireOp",EDGE,"E24.filletArc");Q0=makeQuery(id+"F2.boolean.opBoolean","SPLIT",FACE,{"disambiguationData":[TD([makeQuery(id+"F1.opExtrude","SWEPT_FACE",FACE,{"disambiguationData":[OSD([subQ5])]})])],"derivedFrom":makeQuery(id+"F1.opExtrude","CAP_FACE",FACE,{"disambiguationData":[OSD([subQ5,subQ7,subQ8,subQ9,subQ4,subQ3,subQ2,subQ1,subQ6,subQ0,subQ10,subQ11])],"isStart":true})});}
            var sketch = newSketch(context, id + "F16", { "sketchPlane" : qUnion([Q0])});
            skLineSegment(sketch, "E79", {"start": v(-37, 90) * mm, "end": v(-17.11, 108) * mm});
            skLineSegment(sketch, "E80", {"start": v(-17.11, 108) * mm, "end": v(-17.11, 123.3) * mm});
            skArc(sketch, "E81", {"start": v(12.89, 123.3) * mm, "mid": v(-2.11, 138.3) * mm, "end": v(-17.11, 123.3) * mm});
            skLineSegment(sketch, "E82", {"start": v(12.89, 123.3) * mm, "end": v(12.89, 111.4) * mm});
            skLineSegment(sketch, "E83", {"start": v(12.89, 111.4) * mm, "end": v(34.28, 90) * mm});
            skCircle(sketch, "E84", {"center": v(-2.11, 123.3) * mm, "radius": 6 * mm});
            skLineSegment(sketch, "E85", {"start": v(-80, 0) * mm, "end": v(80, 0) * mm});
            skArc(sketch, "E86.MirrorCS", {"start": v(12.89, -123.3) * mm, "mid": v(-2.11, -138.3) * mm, "end": v(-17.11, -123.3) * mm});
            skLineSegment(sketch, "E87.MirrorCS", {"start": v(-17.11, -108) * mm, "end": v(-17.11, -123.3) * mm});
            skLineSegment(sketch, "E88.MirrorCS", {"start": v(12.89, -123.3) * mm, "end": v(12.89, -111.4) * mm});
            skCircle(sketch, "E89.MirrorC", {"center": v(-2.11, -123.3) * mm, "radius": 6 * mm});
            skLineSegment(sketch, "E90.MirrorCS", {"start": v(-37, -90) * mm, "end": v(-17.11, -108) * mm});
            skLineSegment(sketch, "E91.MirrorCS", {"start": v(12.89, -111.4) * mm, "end": v(34.28, -90) * mm});
            skSolve(sketch);
        }
        {
            var Q0;
            {var subQ0=sQuery(id+"F16.wireOp",EDGE,"E79");Q0=makeQuery(id+"F16.imprint","IMPRINT",FACE,{"disambiguationData":[TD([[makeQuery(id+"F16.imprint","IMPRINT",EDGE,{"derivedFrom":subQ0}),-1.0]])]});}
            var Q1;
            Q1=makeQuery(id+"F16.imprint","IMPRINT",FACE,{"disambiguationData":[TD([[makeQuery(id+"F16.imprint","IMPRINT",EDGE,{"derivedFrom":sQuery(id+"F16.wireOp",EDGE,"E86.MirrorCS")}),-1.0]])]});
            var Q2;
            Q2=makeQuery(id+"F16.imprint","IMPRINT",FACE,{"disambiguationData":[TD([[makeQuery(id+"F16.imprint","IMPRINT",EDGE,{"derivedFrom":makeQuery(id+"F1.opExtrude","CAP_EDGE",EDGE,{"disambiguationData":[OSD([sQuery(id+"F0.wireOp",EDGE,"E6")])],"isStart":true})}),-1.0]])]});
            var Q3;
            Q3=makeQuery(id+"F16.imprint","IMPRINT",FACE,{"disambiguationData":[TD([[makeQuery(id+"F16.imprint","IMPRINT",EDGE,{"derivedFrom":makeQuery(id+"F1.opExtrude","CAP_EDGE",EDGE,{"disambiguationData":[OSD([sQuery(id+"F0.wireOp",EDGE,"E4")])],"isStart":true})}),-1.0]])]});
            var Q4;
            Q4=makeQuery(id+"F2.opExtrude","CAP_FACE",FACE,{"disambiguationData":[OSD([sQuery(id+"F0.wireOp",EDGE,"E12"),sQuery(id+"F0.wireOp",EDGE,"E13"),sQuery(id+"F0.wireOp",EDGE,"E14"),sQuery(id+"F0.wireOp",EDGE,"E15"),sQuery(id+"F0.wireOp",EDGE,"E17.filletArc"),sQuery(id+"F0.wireOp",EDGE,"E18.filletArc"),sQuery(id+"F0.wireOp",EDGE,"E19.filletArc"),sQuery(id+"F0.wireOp",EDGE,"E20.filletArc"),sQuery(id+"F0.wireOp",EDGE,"E25.0"),sQuery(id+"F0.wireOp",EDGE,"E25.1"),sQuery(id+"F0.wireOp",EDGE,"E25.2"),sQuery(id+"F0.wireOp",EDGE,"E25.3"),sQuery(id+"F0.wireOp",EDGE,"E25.4"),sQuery(id+"F0.wireOp",EDGE,"E25.5"),sQuery(id+"F0.wireOp",EDGE,"E25.6"),sQuery(id+"F0.wireOp",EDGE,"E25.7")])],"isStart":false});
            extrude(context, id + "F17", {"entities" : qUnion([Q0, Q1, Q2, Q3]), "endBound" : BoundingType.UP_TO_SURFACE, "endBoundEntityFace" : qUnion([Q4]), "depth" : 25 * mm});
        }
    });
